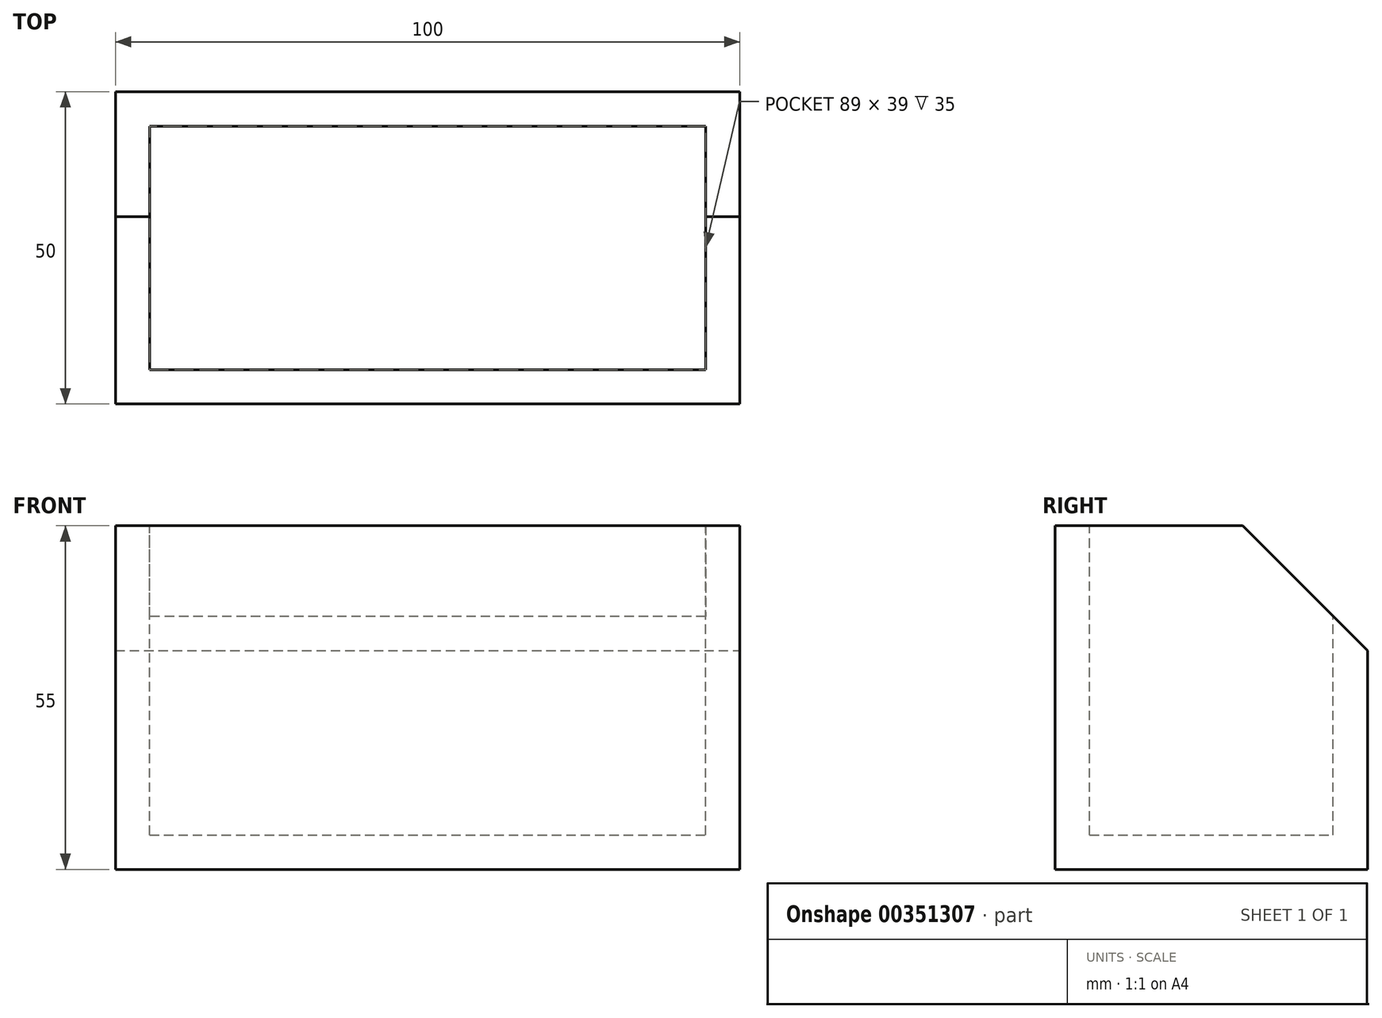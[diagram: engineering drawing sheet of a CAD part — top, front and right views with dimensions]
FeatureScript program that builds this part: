
annotation { "Feature Type Name" : "Feature", "Feature Type Description" : "" }
export const myFeature = defineFeature(function(context is Context, id is Id, definition is map)
    precondition{}
    {
        {
            var Q0;
            Q0=qCreatedBy(makeId("Front.planeOp"),FACE);
            var sketch = newSketch(context, id + "F0", { "sketchPlane" : qUnion([Q0])});
            skLineSegment(sketch, "E0.bottom", {"start": v(-50, -27.5) * mm, "end": v(50, -27.5) * mm});
            skLineSegment(sketch, "E0.top", {"start": v(-50, 27.5) * mm, "end": v(50, 27.5) * mm});
            skLineSegment(sketch, "E0.left", {"start": v(-50, -27.5) * mm, "end": v(-50, 27.5) * mm});
            skLineSegment(sketch, "E0.right", {"start": v(50, -27.5) * mm, "end": v(50, 27.5) * mm});
            skPoint(sketch, "E0.middle", {"position": v(0, 0) * mm});
            skSolve(sketch);
        }
        {
            var Q0;
            Q0=makeQuery(id+"F0.imprint","IMPRINT",FACE,{"disambiguationData":[TD([[makeQuery(id+"F0.imprint","IMPRINT",EDGE,{"derivedFrom":sQuery(id+"F0.wireOp",EDGE,"E0.bottom")}),1.0]])]});
            extrude(context, id + "F1", {"entities" : qUnion([Q0]), "depth" : 50 * mm});
        }
        {
            var Q0;
            Q0=makeQuery(id+"F1.opExtrude","SWEPT_FACE",FACE,{"disambiguationData":[OSD([sQuery(id+"F0.wireOp",EDGE,"E0.top")])]});
            shell(context, id + "F2", {"entities" : qUnion([Q0]), "thickness" : 5.5 * mm});
        }
        {
            var Q0;
            Q0=makeQuery(id+"F1.opExtrude","CAP_EDGE",EDGE,{"disambiguationData":[OSD([sQuery(id+"F0.wireOp",EDGE,"E0.top")])],"isStart":true});
            chamfer(context, id + "F3", {"entities" : qUnion([Q0]), "width" : 20 * mm, "tangentPropagation" : true});
        }
    });
